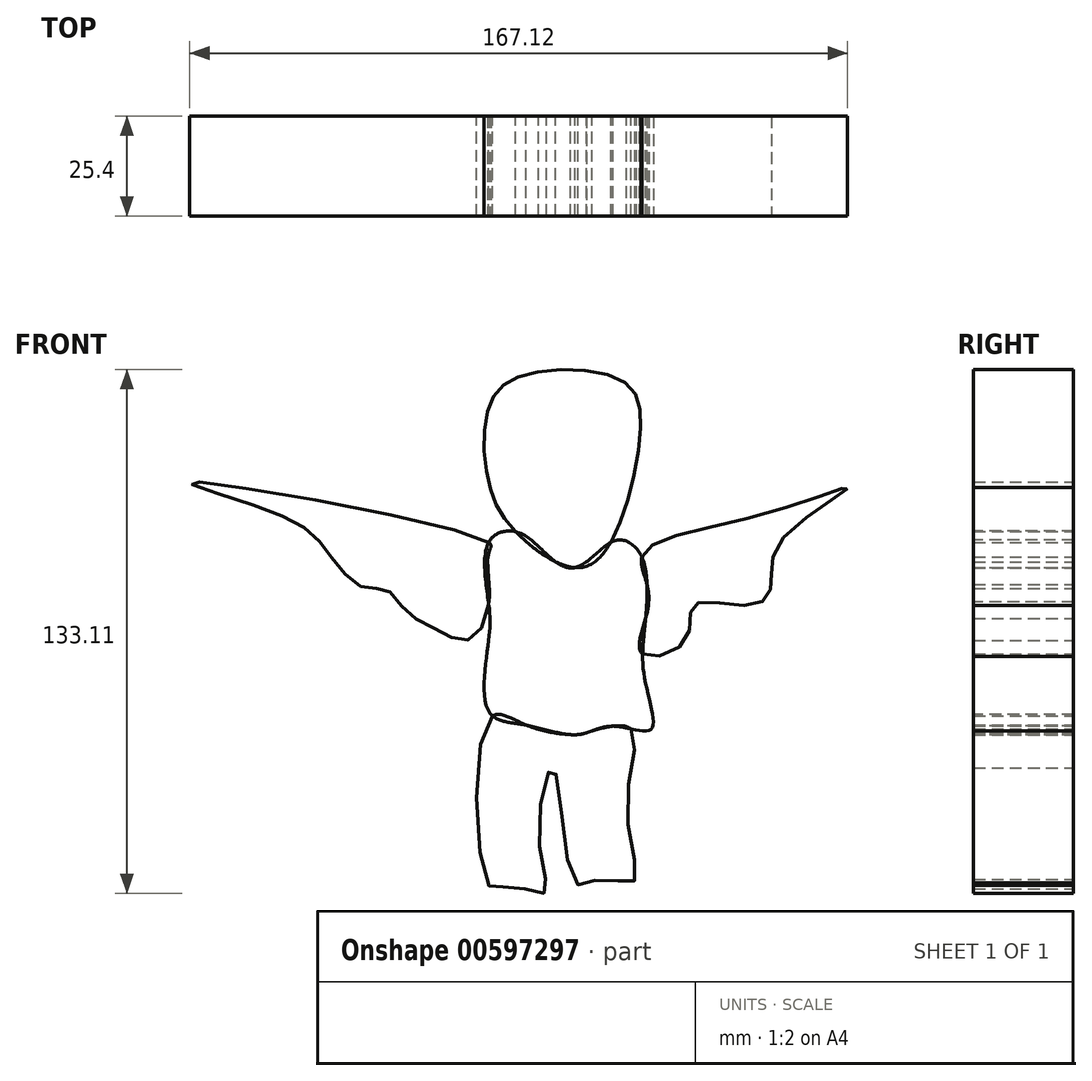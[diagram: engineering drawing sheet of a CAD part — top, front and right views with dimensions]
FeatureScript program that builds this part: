
annotation { "Feature Type Name" : "Feature", "Feature Type Description" : "" }
export const myFeature = defineFeature(function(context is Context, id is Id, definition is map)
    precondition{}
    {
        {
            var Q0;
            Q0=qCreatedBy(makeId("Front.planeOp"),FACE);
            var sketch = newSketch(context, id + "F0", { "sketchPlane" : qUnion([Q0])});
            skFitSpline(sketch, "E0", {"points": [v(0, 24.84) * mm, v(-75.58, 40.14) * mm, v(-62.16, 35.04) * mm, v(-45.24, 27.25) * mm, v(-38.8, 19.47) * mm, v(-31.55, 13.3) * mm, v(-25.9, 12.75) * mm, v(-20.8, 7.11) * mm, v(-12.48, 2.28) * mm, v(-5.24, 0) * mm, v(0, 9) * mm, v(0, 22.15) * mm, v(0, 24.84) * mm]});
            skFitSpline(sketch, "E1", {"points": [v(0, 24.84) * mm, v(6.85, 27.52) * mm, v(14.36, 22.15) * mm, v(21.88, 18.4) * mm, v(31.01, 24.84) * mm, v(35.57, 24.84) * mm, v(39.33, 20) * mm, v(39.87, 5.5) * mm, v(39.6, -9.8) * mm, v(41.21, -22.69) * mm, v(31.55, -21.88) * mm, v(22.69, -24.03) * mm, v(9.53, -21.61) * mm, v(0, -18.12) * mm, v(0, 0) * mm, v(0, 9) * mm, v(0, 24.84) * mm]});
            skFitSpline(sketch, "E2", {"points": [v(39.33, 22.15) * mm, v(69.4, 31.82) * mm, v(91.15, 38.53) * mm, v(73.97, 24.84) * mm, v(71.82, 14.36) * mm, v(67.53, 9) * mm, v(52.22, 9) * mm, v(50.07, 0) * mm, v(39.12, -3.57) * mm, v(39.87, 5.5) * mm, v(40.22, 14.11) * mm, v(39.33, 22.15) * mm]});
            skFitSpline(sketch, "E3", {"points": [v(0, -20.27) * mm, v(0, -62.42) * mm, v(5.24, -62.42) * mm, v(14.1, -64.3) * mm, v(12.75, -50.61) * mm, v(16.51, -32.62) * mm, v(21.88, -61.62) * mm, v(28.33, -60.81) * mm, v(36.92, -61.35) * mm, v(35.04, -42.29) * mm, v(36.19, -22.6) * mm, v(26.23, -23.1) * mm, v(22.69, -24.03) * mm, v(9.53, -21.61) * mm, v(0, -20.27) * mm]});
            skFitSpline(sketch, "E4", {"points": [v(6.85, 27.52) * mm, v(0, 39.87) * mm, v(0, 59.2) * mm, v(9.53, 67.53) * mm, v(34.23, 65.65) * mm, v(38.53, 52.76) * mm, v(31.01, 24.84) * mm, v(21.88, 18.4) * mm, v(6.85, 27.52) * mm]});
            skSolve(sketch);
        }
        {
            var Q0;
            {var subQ0=sQuery(id+"F0.wireOp",EDGE,"E4");var subQ1=sQuery(id+"F0.wireOp",EDGE,"E1");var subQ2=makeQuery(id+"F0.imprint","INTERSECT",VERTEX,{"disambiguationData":[OD(0.0)],"derivedFrom":[subQ1,subQ0]});Q0=makeQuery(id+"F0.imprint","IMPRINT",FACE,{"disambiguationData":[TD([[makeQuery(id+"F0.imprint","IMPRINT",EDGE,{"disambiguationData":[TD([[subQ2,-1.0]])],"derivedFrom":subQ1}),1.0]])]});}
            var Q1;
            {var subQ0=sQuery(id+"F0.wireOp",EDGE,"E1");var subQ1=sQuery(id+"F0.wireOp",EDGE,"E0");var subQ2=makeQuery(id+"F0.imprint","INTERSECT",VERTEX,{"disambiguationData":[OD(0.0)],"derivedFrom":[subQ1,subQ0]});Q1=makeQuery(id+"F0.imprint","IMPRINT",FACE,{"disambiguationData":[TD([[makeQuery(id+"F0.imprint","IMPRINT",EDGE,{"disambiguationData":[TD([[subQ2,-1.0]])],"derivedFrom":subQ1}),1.0]])]});}
            var Q2;
            {var subQ0=sQuery(id+"F0.wireOp",EDGE,"E1");var subQ1=sQuery(id+"F0.wireOp",EDGE,"E0");var subQ21=makeQuery(id+"F0.imprint","INTERSECT",VERTEX,{"disambiguationData":[OD(0.0)],"derivedFrom":[subQ1,subQ0]});Q2=makeQuery(id+"F0.imprint","IMPRINT",FACE,{"disambiguationData":[TD([[makeQuery(id+"F0.imprint","IMPRINT",EDGE,{"disambiguationData":[TD([[subQ21,1.0]])],"derivedFrom":subQ1}),-1.0]])]});}
            var Q3;
            {var subQ0=sQuery(id+"F0.wireOp",EDGE,"E3");var subQ1=sQuery(id+"F0.wireOp",EDGE,"E1");var subQ8=makeQuery(id+"F0.imprint","INTERSECT",VERTEX,{"disambiguationData":[OD(0.0)],"derivedFrom":[subQ1,subQ0]});Q3=makeQuery(id+"F0.imprint","IMPRINT",FACE,{"disambiguationData":[TD([[makeQuery(id+"F0.imprint","IMPRINT",EDGE,{"disambiguationData":[TD([[subQ8,-1.0]])],"derivedFrom":subQ1}),1.0]])]});}
            var Q4;
            {var subQ0=sQuery(id+"F0.wireOp",EDGE,"E2");var subQ1=sQuery(id+"F0.wireOp",EDGE,"E1");var subQ2=makeQuery(id+"F0.imprint","INTERSECT",VERTEX,{"disambiguationData":[OD(0.0)],"derivedFrom":[subQ1,subQ0]});Q4=makeQuery(id+"F0.imprint","IMPRINT",FACE,{"disambiguationData":[TD([[makeQuery(id+"F0.imprint","IMPRINT",EDGE,{"disambiguationData":[TD([[subQ2,-1.0]])],"derivedFrom":subQ1}),1.0]])]});}
            extrude(context, id + "F1", {"entities" : qUnion([Q0, Q1, Q2, Q3, Q4]), "depth" : 25.4 * mm, "offsetDistance" : 25.4 * mm});
        }
    });
